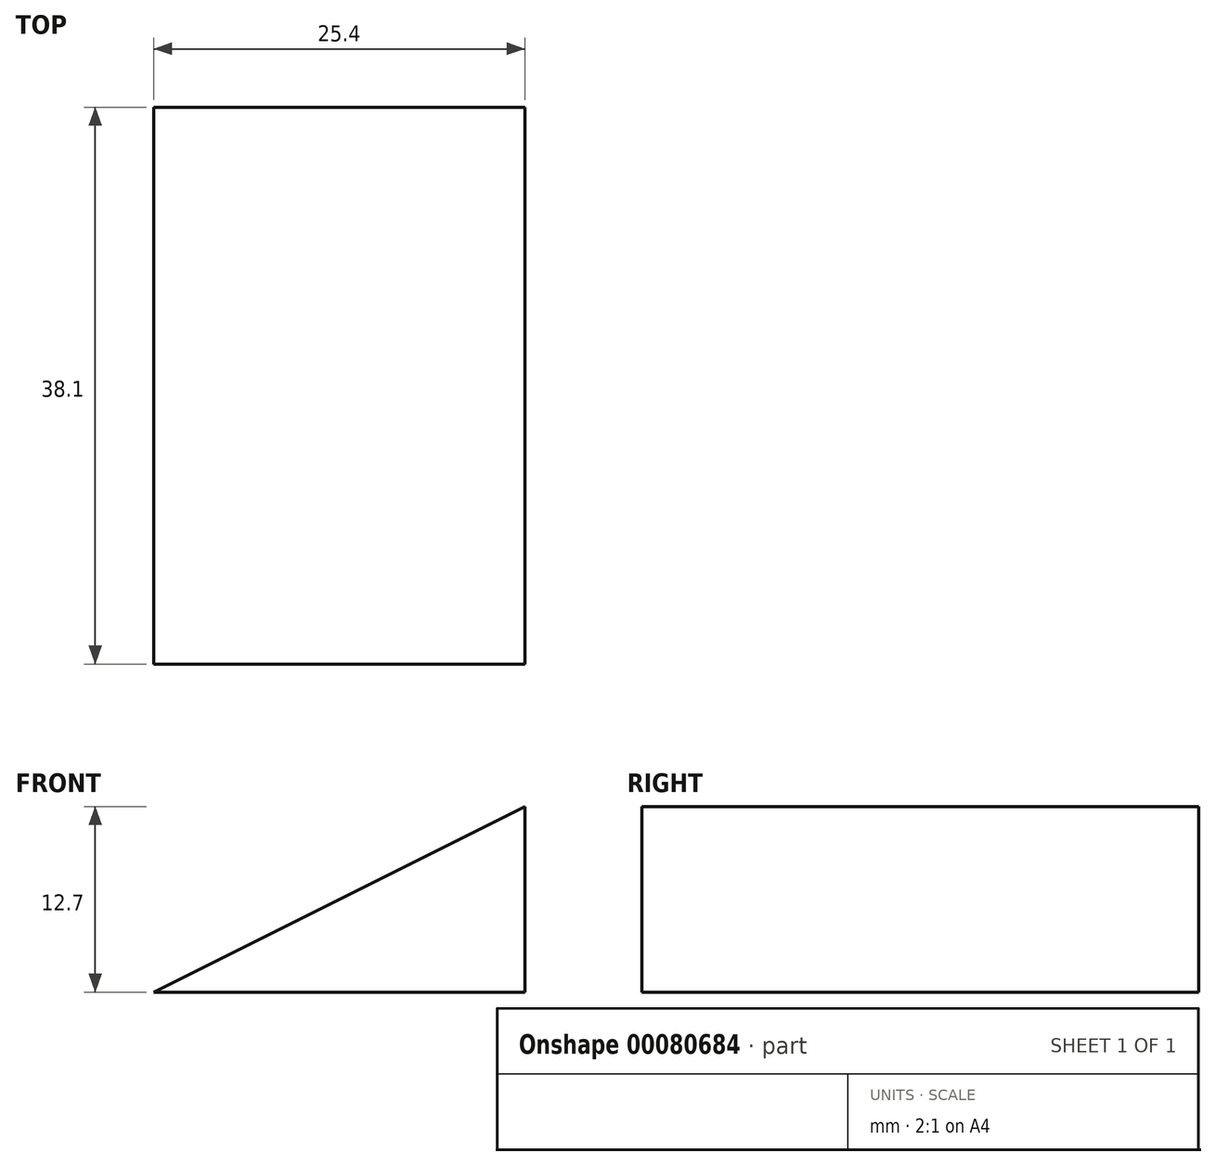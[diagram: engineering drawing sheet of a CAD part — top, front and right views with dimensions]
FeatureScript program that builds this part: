
annotation { "Feature Type Name" : "Feature", "Feature Type Description" : "" }
export const myFeature = defineFeature(function(context is Context, id is Id, definition is map)
    precondition{}
    {
        {
            var Q0;
            Q0=qCreatedBy(makeId("Front.planeOp"),FACE);
            var sketch = newSketch(context, id + "F0", { "sketchPlane" : qUnion([Q0])});
            skLineSegment(sketch, "E0", {"start": v(0, 12.7) * mm, "end": v(0, 0) * mm});
            skLineSegment(sketch, "E1", {"start": v(0, 0) * mm, "end": v(-25.4, 0) * mm});
            skLineSegment(sketch, "E2", {"start": v(0, 12.7) * mm, "end": v(-25.4, 0) * mm});
            skSolve(sketch);
        }
        {
            var Q0;
            Q0=makeQuery(id+"F0.imprint","IMPRINT",FACE,{"disambiguationData":[TD([[makeQuery(id+"F0.imprint","IMPRINT",EDGE,{"derivedFrom":sQuery(id+"F0.wireOp",EDGE,"E0")}),-1.0]])]});
            extrude(context, id + "F1", {"entities" : qUnion([Q0]), "depth" : 38.1 * mm, "symmetric" : true});
        }
    });
